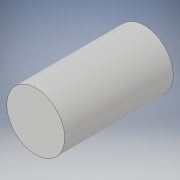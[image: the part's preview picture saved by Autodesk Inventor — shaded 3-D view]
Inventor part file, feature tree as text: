
AUTODESK INVENTOR PART (.ipt)
format: ipt  version: 2019 (Build 230136000, 136)  size: 88,576 bytes
history: native  units: mm
features: extrude x1, sketch x1
ambient origin geometry x8: Origin, YZ Plane, XZ Plane, XY Plane, X Axis, Y Axis, Z Axis, Center Point
bodies: Solid1 (feature_tree)
feature tree (2):
  extrude  "Extrusion1"  Depth=15.0mm TaperAngle=0.0deg
  sketch  "Sketch1"  dims[d0=8.0mm d1=15.0mm d2=0.0mm]
